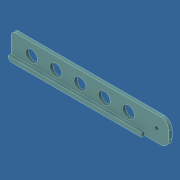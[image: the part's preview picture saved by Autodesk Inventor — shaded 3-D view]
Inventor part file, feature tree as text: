
AUTODESK INVENTOR PART (.ipt)
format: ipt  version: 2018 (Build 220112000, 112)  size: 144,384 bytes
history: native  units: in
note: dims shown in document units (in); Inventor stores cm internally (conversion verified against a paired STEP export)
features: sketch x5, extrude x2, hole x2, fillet x2, pattern_linear x1
ambient origin geometry x8: Origin, YZ Plane, XZ Plane, XY Plane, X Axis, Y Axis, Z Axis, Center Point
bodies: Solid1 (feature_tree)
feature tree (12):
  sketch  "Sketch1"  dims[d0=0.6in d1=3.9in]
  extrude  "Extrusion1"  Depth=3.9in
  hole  "Hole1"  [1 undecoded]
  pattern_linear  "Rectangular Pattern1"  Spacing1=3.3in  [1 undecoded]
  hole  "Hole2"  [1 undecoded]
  extrude  "Extrusion2"  Depth=0.08in TaperAngle=0.0deg
  fillet  "Fillet1"  Radius=0.2in
  fillet  "Fillet2"  Radius=0.1in
  sketch  "Sketch2"  dims[d2=0.08in d3=0.0in]
  sketch  "Sketch3"  dims[d4=0.3in d5=0.75in d6=0.375in d7=0.25in d8=0.5635in d9=1.0in d10=0.8108in d11=1.9685in d13=0.6in]
  sketch  "Sketch4"  dims[d14=0.5in]
  sketch  "Sketch5"  dims[d15=0.3in d16=0.1in d17=0.75in d18=0.375in d19=0.25in d20=0.5635in d21=1.0in d22=0.8108in d23=3.3in d24=0.1in d25=0.08in d26=0.0in d27=0.2in d28=0.1in]
note: 3 required parameter values undecoded (feature->parameter linkage not recoverable at this tier; creation-order binding heuristic only, values carry confidence <= 0.55)
